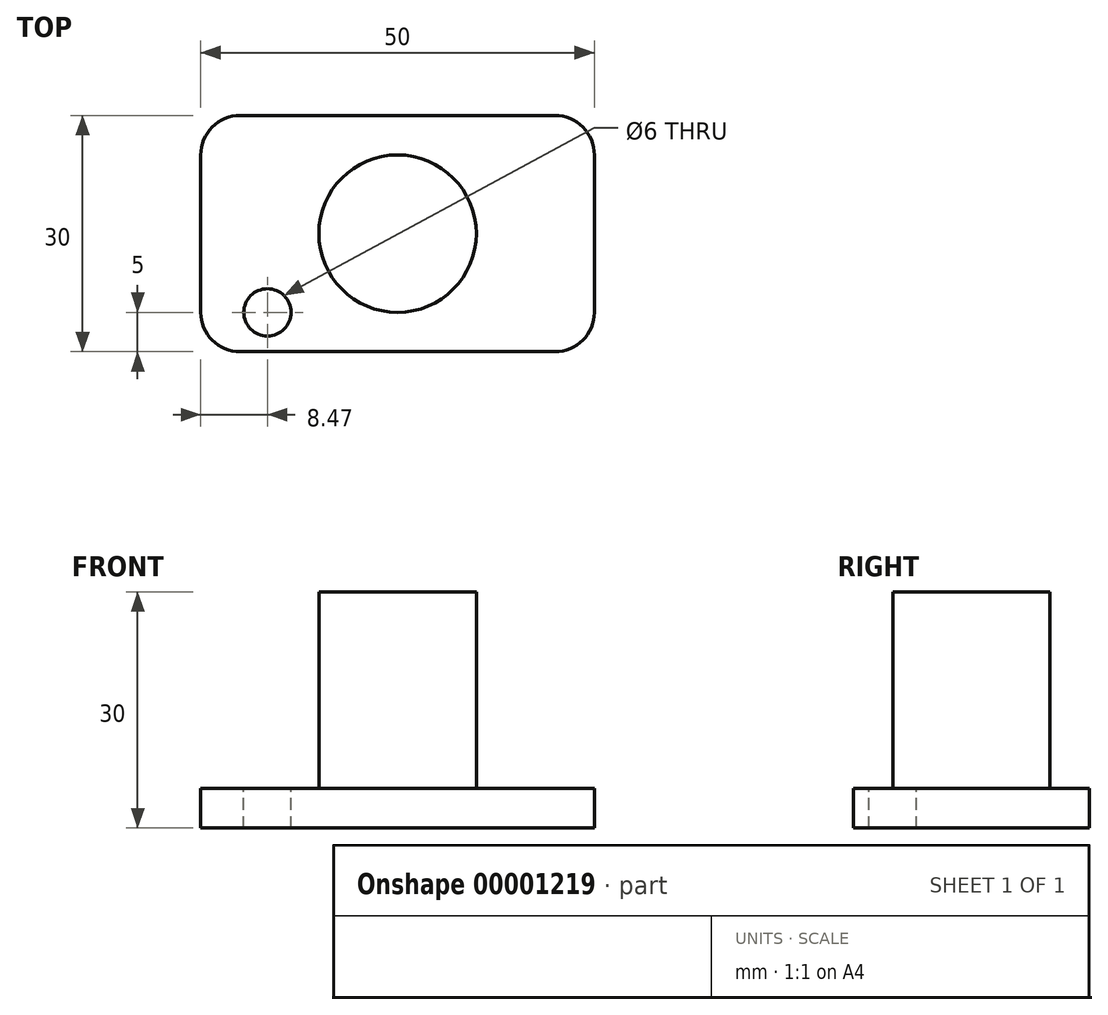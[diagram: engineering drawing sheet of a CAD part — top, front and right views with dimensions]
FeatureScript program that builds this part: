
annotation { "Feature Type Name" : "Feature", "Feature Type Description" : "" }
export const myFeature = defineFeature(function(context is Context, id is Id, definition is map)
    precondition{}
    {
        {
            var Q0;
            Q0=qCreatedBy(makeId("Top.planeOp"),FACE);
            var sketch = newSketch(context, id + "F0", { "sketchPlane" : qUnion([Q0])});
            skLineSegment(sketch, "E0.bottom", {"start": v(0, 0) * mm, "end": v(50, 0) * mm});
            skLineSegment(sketch, "E0.top", {"start": v(0, 30) * mm, "end": v(50, 30) * mm});
            skLineSegment(sketch, "E0.left", {"start": v(0, 0) * mm, "end": v(0, 30) * mm});
            skLineSegment(sketch, "E0.right", {"start": v(50, 0) * mm, "end": v(50, 30) * mm});
            skSolve(sketch);
        }
        {
            var Q0;
            Q0=makeQuery(id+"F0.imprint","IMPRINT",FACE,{"disambiguationData":[TD([[makeQuery(id+"F0.imprint","IMPRINT",EDGE,{"derivedFrom":sQuery(id+"F0.wireOp",EDGE,"E0.bottom")}),1.0]])]});
            extrude(context, id + "F1", {"entities" : qUnion([Q0]), "depth" : 5 * mm});
        }
        {
            var Q0;
            Q0=makeQuery(id+"F1.opExtrude","CAP_FACE",FACE,{"disambiguationData":[OSD([sQuery(id+"F0.wireOp",EDGE,"E0.bottom"),sQuery(id+"F0.wireOp",EDGE,"E0.top"),sQuery(id+"F0.wireOp",EDGE,"E0.left"),sQuery(id+"F0.wireOp",EDGE,"E0.right")])],"isStart":false});
            var sketch = newSketch(context, id + "F2", { "sketchPlane" : qUnion([Q0])});
            skCircle(sketch, "E1", {"center": v(25, 15) * mm, "radius": 10 * mm});
            skSolve(sketch);
        }
        {
            var Q0;
            Q0=makeQuery(id+"F2.imprint","IMPRINT",FACE,{"disambiguationData":[TD([[makeQuery(id+"F2.imprint","IMPRINT",EDGE,{"derivedFrom":sQuery(id+"F2.wireOp",EDGE,"E1")}),1.0]])]});
            extrude(context, id + "F3", {"entities" : qUnion([Q0]), "operationType" : NewBodyOperationType.ADD, "depth" : 25 * mm});
        }
        {
            var Q0;
            Q0=makeQuery(id+"F1.opExtrude","SWEPT_EDGE",EDGE,{"disambiguationData":[OSD([sQuery(id+"F0.wireOp",EDGE,"E0.bottom"),sQuery(id+"F0.wireOp",EDGE,"E0.right")])]});
            var Q1;
            Q1=makeQuery(id+"F1.opExtrude","SWEPT_EDGE",EDGE,{"disambiguationData":[OSD([sQuery(id+"F0.wireOp",EDGE,"E0.top"),sQuery(id+"F0.wireOp",EDGE,"E0.right")])]});
            var Q2;
            Q2=makeQuery(id+"F1.opExtrude","SWEPT_EDGE",EDGE,{"disambiguationData":[OSD([sQuery(id+"F0.wireOp",EDGE,"E0.bottom"),sQuery(id+"F0.wireOp",EDGE,"E0.left")])]});
            var Q3;
            Q3=makeQuery(id+"F1.opExtrude","SWEPT_EDGE",EDGE,{"disambiguationData":[OSD([sQuery(id+"F0.wireOp",EDGE,"E0.top"),sQuery(id+"F0.wireOp",EDGE,"E0.left")])]});
            fillet(context, id + "F4", {"entities" : qUnion([Q0, Q1, Q2, Q3]), "radius" : 5 * mm, "tangentPropagation" : true, "allowEdgeOverflow" : false});
        }
        {
            var Q0;
            Q0=makeQuery(id+"F1.opExtrude","CAP_FACE",FACE,{"disambiguationData":[OSD([sQuery(id+"F0.wireOp",EDGE,"E0.bottom"),sQuery(id+"F0.wireOp",EDGE,"E0.top"),sQuery(id+"F0.wireOp",EDGE,"E0.left"),sQuery(id+"F0.wireOp",EDGE,"E0.right")])],"isStart":false});
            var sketch = newSketch(context, id + "F5", { "sketchPlane" : qUnion([Q0])});
            skCircle(sketch, "E2", {"center": v(8.47, 5) * mm, "radius": 3 * mm});
            skSolve(sketch);
        }
        {
            var Q0;
            Q0=makeQuery(id+"F5.imprint","IMPRINT",FACE,{"disambiguationData":[TD([[makeQuery(id+"F5.imprint","IMPRINT",EDGE,{"derivedFrom":sQuery(id+"F5.wireOp",EDGE,"E2")}),1.0]])]});
            extrude(context, id + "F6", {"entities" : qUnion([Q0]), "operationType" : NewBodyOperationType.REMOVE, "endBound" : BoundingType.THROUGH_ALL, "oppositeDirection" : true, "depth" : 25 * mm});
        }
        {
            var Q0;
            Q0=makeQuery(id+"F3.opExtrude","CAP_FACE",FACE,{"disambiguationData":[OSD([sQuery(id+"F2.wireOp",EDGE,"E1")])],"isStart":false});
            var sketch = newSketch(context, id + "F7", { "sketchPlane" : qUnion([Q0])});
            skSolve(sketch);
        }
        {
            var Q0;
            Q0=makeQuery(id+"F7.imprint","IMPRINT",FACE,{"disambiguationData":[TD([[makeQuery(id+"F7.imprint","IMPRINT",EDGE,{"derivedFrom":makeQuery(id+"F3.opExtrude","CAP_EDGE",EDGE,{"disambiguationData":[OSD([sQuery(id+"F2.wireOp",EDGE,"E1")])],"isStart":false})}),1.0]])]});
            var sketch = newSketch(context, id + "F8", { "sketchPlane" : qUnion([Q0])});
            skSolve(sketch);
        }
        {
            var Q0;
            Q0=makeQuery(id+"F8.imprint","IMPRINT",FACE,{"disambiguationData":[TD([[makeQuery(id+"F8.imprint","IMPRINT",EDGE,{"derivedFrom":makeQuery(id+"F7.imprint","IMPRINT",EDGE,{"derivedFrom":makeQuery(id+"F3.opExtrude","CAP_EDGE",EDGE,{"disambiguationData":[OSD([sQuery(id+"F2.wireOp",EDGE,"E1")])],"isStart":false})})}),1.0]])]});
            var sketch = newSketch(context, id + "F9", { "sketchPlane" : qUnion([Q0])});
            skPoint(sketch, "E3", {"position": v(26.14, 18.13) * mm});
            skCircle(sketch, "E4.0", {"center": v(25, 15) * mm, "radius": 10 * mm});
            skCircle(sketch, "E5", {"center": v(25, 15) * mm, "radius": 6 * mm});
            skSolve(sketch);
        }
        {
            var Q0;
            Q0=sQuery(id+"F9.wireOp",EDGE,"E5");
            extrude(context, id + "F10", {"bodyType" : ToolBodyType.SURFACE, "surfaceEntities" : qUnion([Q0]), "depth" : 25 * mm});
        }
        {
            var Q0;
            Q0=makeQuery(id+"F10.opExtrude","SWEPT_FACE",FACE,{"disambiguationData":[OSD([sQuery(id+"F9.wireOp",EDGE,"E5")])]});
            var Q1;
            Q1=makeQuery(id+"F1.opExtrude","CAP_EDGE",EDGE,{"disambiguationData":[OSD([sQuery(id+"F0.wireOp",EDGE,"E0.bottom")])],"isStart":false});
            circularPattern(context, id + "F11", {"faces" : qUnion([Q0]), "axis" : qUnion([Q1]), "angle" : 30 * degree, "instanceCount" : 12, "patternType" : PatternType.FACE});
        }
    });
